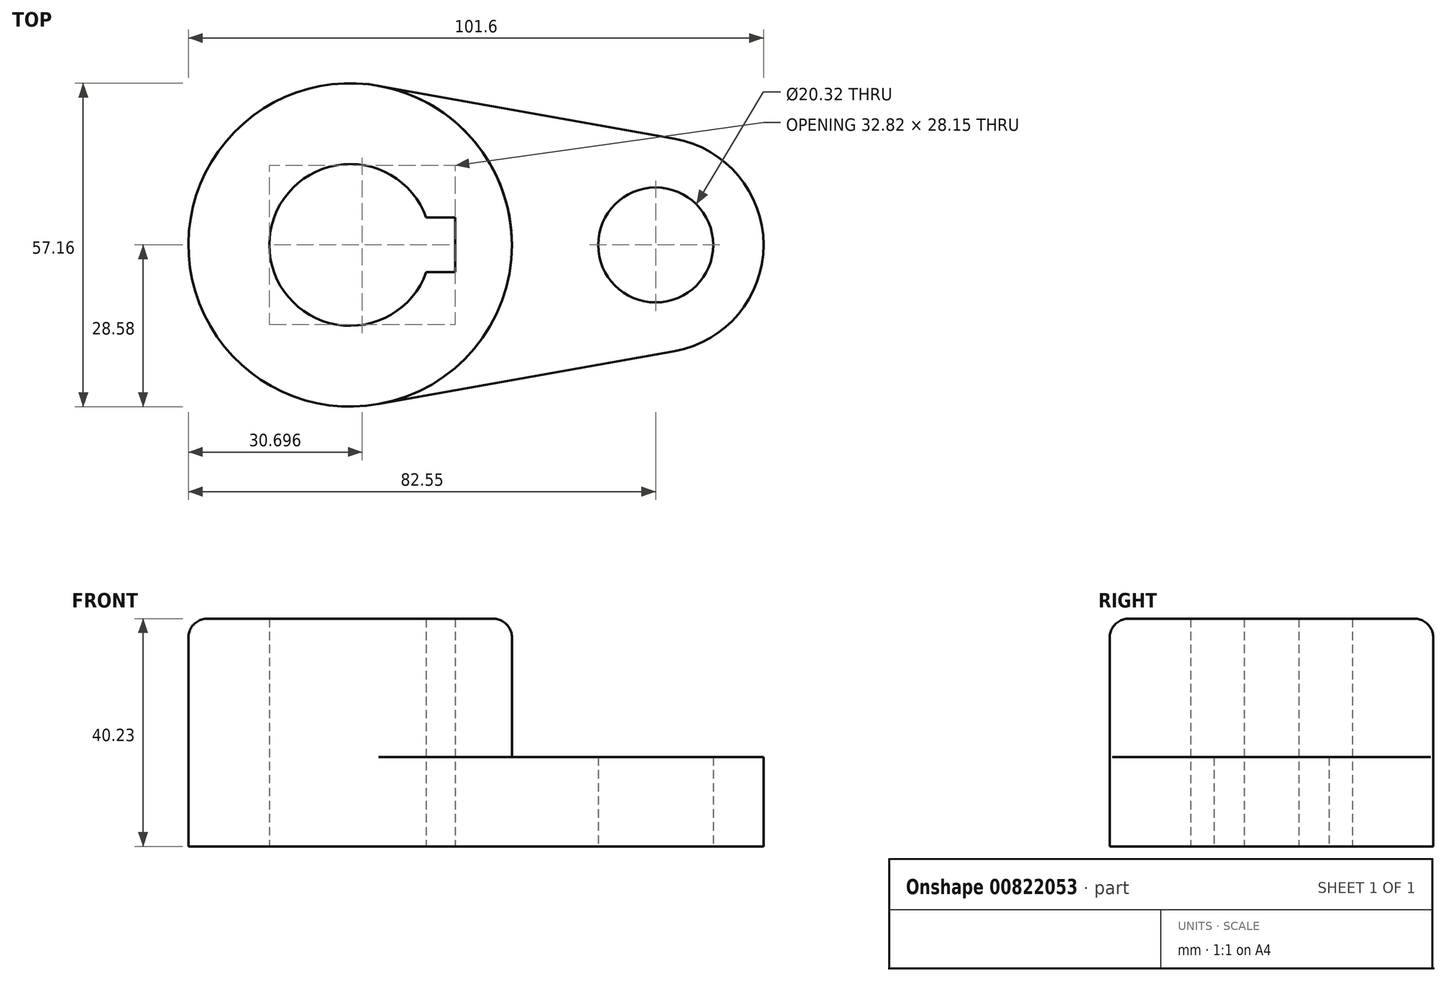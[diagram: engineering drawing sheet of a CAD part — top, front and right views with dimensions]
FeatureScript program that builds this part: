
annotation { "Feature Type Name" : "Feature", "Feature Type Description" : "" }
export const myFeature = defineFeature(function(context is Context, id is Id, definition is map)
    precondition{}
    {
        {
            var Q0;
            Q0=qCreatedBy(makeId("Top.planeOp"),FACE);
            var sketch = newSketch(context, id + "F0", { "sketchPlane" : qUnion([Q0])});
            skCircle(sketch, "E0", {"center": v(-53.98, 0) * mm, "radius": 28.58 * mm});
            skCircle(sketch, "E1", {"center": v(0, 0) * mm, "radius": 10.16 * mm});
            skArc(sketch, "E2", {"start": v(-40.53, 4.83) * mm, "mid": v(-68.26, 0) * mm, "end": v(-40.53, -4.83) * mm});
            skLineSegment(sketch, "E3", {"start": v(3.36, 18.75) * mm, "end": v(-48.93, 28.13) * mm});
            skLineSegment(sketch, "E4", {"start": v(-48.93, -28.13) * mm, "end": v(3.36, -18.75) * mm});
            skLineSegment(sketch, "E5", {"start": v(-40.53, -4.83) * mm, "end": v(-35.45, -4.83) * mm});
            skLineSegment(sketch, "E6", {"start": v(-35.45, -4.83) * mm, "end": v(-35.45, 4.83) * mm});
            skLineSegment(sketch, "E7", {"start": v(-35.45, 4.83) * mm, "end": v(-40.53, 4.83) * mm});
            skArc(sketch, "E8", {"start": v(3.36, -18.75) * mm, "mid": v(19.05, 0) * mm, "end": v(3.36, 18.75) * mm});
            skSolve(sketch);
        }
        {
            var Q0;
            Q0=makeQuery(id+"F0.imprint","IMPRINT",FACE,{"disambiguationData":[TD([[makeQuery(id+"F0.imprint","IMPRINT",EDGE,{"derivedFrom":sQuery(id+"F0.wireOp",EDGE,"E1")}),-1.0]])]});
            extrude(context, id + "F1", {"entities" : qUnion([Q0]), "depth" : 15.77 * mm, "offsetDistance" : 25.4 * mm});
        }
        {
            var Q0;
            Q0=makeQuery(id+"F0.imprint","IMPRINT",FACE,{"disambiguationData":[TD([[makeQuery(id+"F0.imprint","IMPRINT",EDGE,{"derivedFrom":sQuery(id+"F0.wireOp",EDGE,"E2")}),-1.0]])]});
            extrude(context, id + "F2", {"entities" : qUnion([Q0]), "operationType" : NewBodyOperationType.ADD, "depth" : 40.23 * mm, "offsetDistance" : 25.4 * mm});
        }
        {
            var Q0;
            Q0=makeQuery(id+"F2.opExtrude","CAP_EDGE",EDGE,{"disambiguationData":[OSD([sQuery(id+"F0.wireOp",EDGE,"E0")])],"isStart":false});
            fillet(context, id + "F3", {"entities" : qUnion([Q0]), "radius" : 3.3 * mm, "tangentPropagation" : true, "allowEdgeOverflow" : false});
        }
    });
